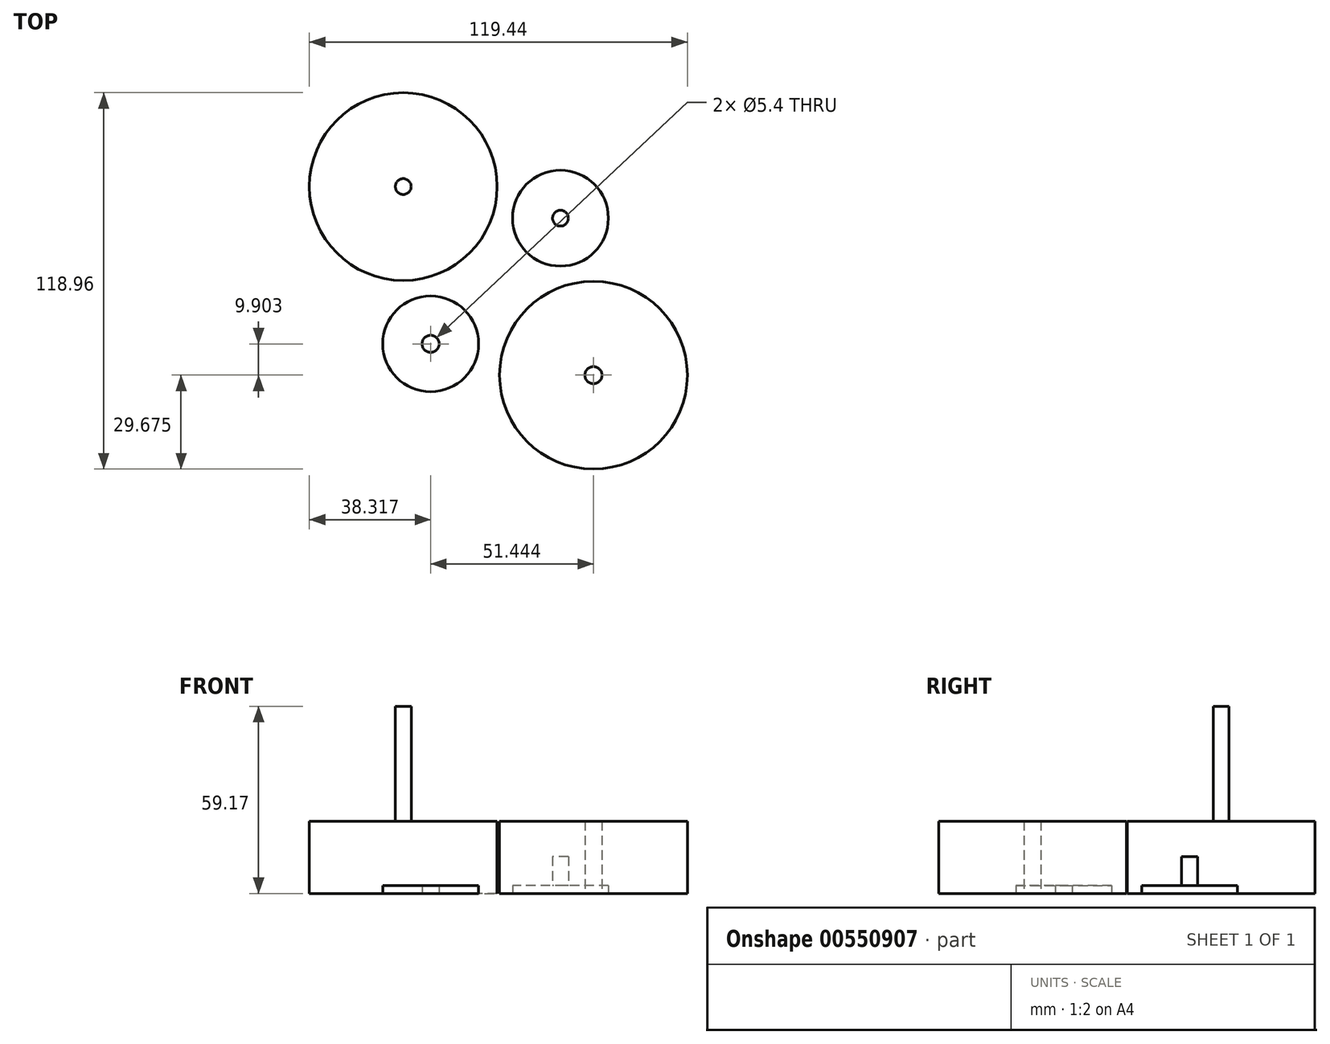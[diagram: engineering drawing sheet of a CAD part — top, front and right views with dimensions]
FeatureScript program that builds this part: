
annotation { "Feature Type Name" : "Feature", "Feature Type Description" : "" }
export const myFeature = defineFeature(function(context is Context, id is Id, definition is map)
    precondition{}
    {
        {
            var Q0;
            Q0=qCreatedBy(makeId("Top.planeOp"),FACE);
            var sketch = newSketch(context, id + "F0", { "sketchPlane" : qUnion([Q0])});
            skCircle(sketch, "E0", {"center": v(-30.15, 30.09) * mm, "radius": 29.68 * mm});
            skCircle(sketch, "E1", {"center": v(19.5, 20.1) * mm, "radius": 15.15 * mm});
            skCircle(sketch, "E2", {"center": v(29.94, -29.53) * mm, "radius": 29.68 * mm});
            skCircle(sketch, "E3", {"center": v(-21.5, -19.62) * mm, "radius": 15.15 * mm});
            skCircle(sketch, "E4", {"center": v(19.5, 20.1) * mm, "radius": 2.5 * mm});
            skCircle(sketch, "E5", {"center": v(-30.15, 30.09) * mm, "radius": 2.5 * mm});
            skSolve(sketch);
        }
        {
            var Q0;
            Q0=makeQuery(id+"F0.imprint","IMPRINT",FACE,{"disambiguationData":[TD([[makeQuery(id+"F0.imprint","IMPRINT",EDGE,{"derivedFrom":sQuery(id+"F0.wireOp",EDGE,"E5")}),1.0]])]});
            extrude(context, id + "F1", {"entities" : qUnion([Q0]), "depth" : 59.17 * mm, "offsetDistance" : 25 * mm});
        }
        {
            var Q0;
            Q0=makeQuery(id+"F0.imprint","IMPRINT",FACE,{"disambiguationData":[TD([[makeQuery(id+"F0.imprint","IMPRINT",EDGE,{"derivedFrom":sQuery(id+"F0.wireOp",EDGE,"E0")}),1.0]])]});
            extrude(context, id + "F2", {"entities" : qUnion([Q0]), "operationType" : NewBodyOperationType.ADD, "depth" : 22.87 * mm, "offsetDistance" : 25 * mm});
        }
        {
            var Q0;
            Q0=makeQuery(id+"F0.imprint","IMPRINT",FACE,{"disambiguationData":[TD([[makeQuery(id+"F0.imprint","IMPRINT",EDGE,{"derivedFrom":sQuery(id+"F0.wireOp",EDGE,"E4")}),1.0]])]});
            extrude(context, id + "F3", {"entities" : qUnion([Q0]), "depth" : 11.66 * mm, "offsetDistance" : 25 * mm});
        }
        {
            var Q0;
            Q0=makeQuery(id+"F0.imprint","IMPRINT",FACE,{"disambiguationData":[TD([[makeQuery(id+"F0.imprint","IMPRINT",EDGE,{"derivedFrom":sQuery(id+"F0.wireOp",EDGE,"E1")}),1.0]])]});
            extrude(context, id + "F4", {"entities" : qUnion([Q0]), "operationType" : NewBodyOperationType.ADD, "depth" : 2.5 * mm, "offsetDistance" : 25 * mm});
        }
        {
            var Q0;
            Q0=makeQuery(id+"F0.imprint","IMPRINT",FACE,{"disambiguationData":[TD([[makeQuery(id+"F0.imprint","IMPRINT",EDGE,{"derivedFrom":sQuery(id+"F0.wireOp",EDGE,"E3")}),1.0]])]});
            extrude(context, id + "F5", {"entities" : qUnion([Q0]), "depth" : 2.5 * mm, "offsetDistance" : 25 * mm});
        }
        {
            var Q0;
            Q0=makeQuery(id+"F0.imprint","IMPRINT",FACE,{"disambiguationData":[TD([[makeQuery(id+"F0.imprint","IMPRINT",EDGE,{"derivedFrom":sQuery(id+"F0.wireOp",EDGE,"E2")}),1.0]])]});
            extrude(context, id + "F6", {"entities" : qUnion([Q0]), "depth" : 22.87 * mm, "offsetDistance" : 25 * mm});
        }
        {
            var Q0;
            Q0=sQuery(id+"F0.wireOp",VERTEX,"E3.center");
            var Q1;
            Q1=makeQuery(id+"F5.opExtrude","SWEPT_BODY",BODY,{"disambiguationData":[OSD([sQuery(id+"F0.wireOp",EDGE,"E3")])]});
            hole(context, id + "F7", {"style" : HoleStyle.SIMPLE, "endStyle" : HoleEndStyle.THROUGH, "oppositeDirection" : true, "holeDiameter" : 5.4 * mm, "isTappedThrough" : true, "tappedDepth" : 12 * mm, "tapClearance" : 3, "locations" : qUnion([Q0]), "scope" : qUnion([Q1]), "majorDiameter" : 5 * mm});
        }
        {
            var Q0;
            Q0=sQuery(id+"F0.wireOp",VERTEX,"E2.center");
            var Q1;
            Q1=makeQuery(id+"F6.opExtrude","SWEPT_BODY",BODY,{"disambiguationData":[OSD([sQuery(id+"F0.wireOp",EDGE,"E2")])]});
            hole(context, id + "F8", {"style" : HoleStyle.SIMPLE, "endStyle" : HoleEndStyle.THROUGH, "oppositeDirection" : true, "holeDiameter" : 5.4 * mm, "isTappedThrough" : true, "tappedDepth" : 12 * mm, "tapClearance" : 3, "locations" : qUnion([Q0]), "scope" : qUnion([Q1]), "majorDiameter" : 5 * mm});
        }
    });
